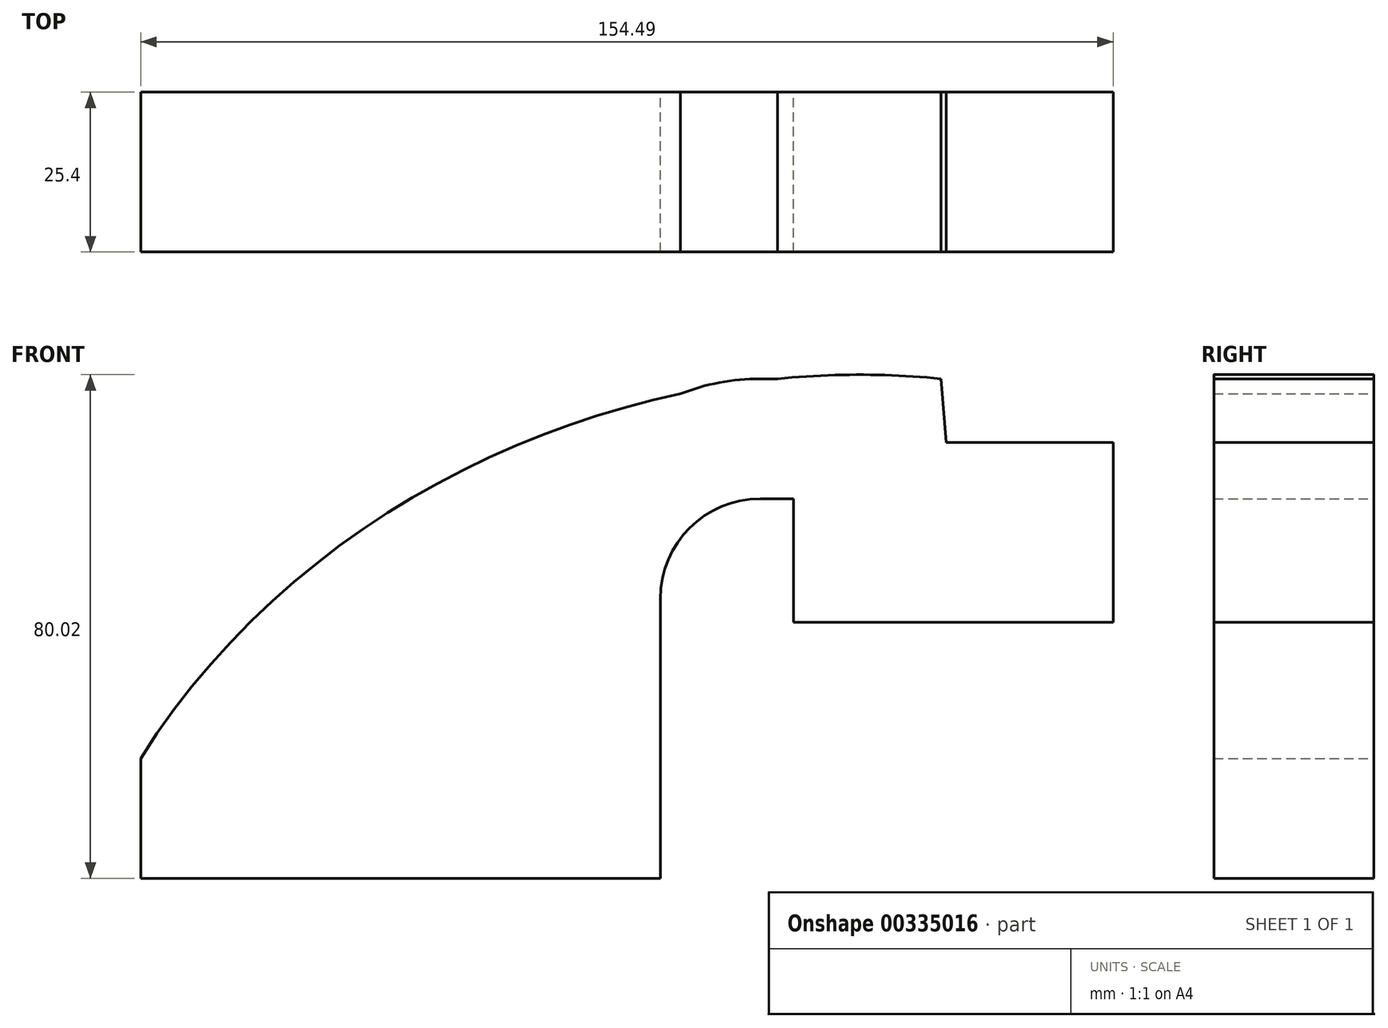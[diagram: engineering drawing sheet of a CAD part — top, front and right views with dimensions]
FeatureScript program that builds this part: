
annotation { "Feature Type Name" : "Feature", "Feature Type Description" : "" }
export const myFeature = defineFeature(function(context is Context, id is Id, definition is map)
    precondition{}
    {
        {
            var Q0;
            Q0=qCreatedBy(makeId("Front.planeOp"),FACE);
            var sketch = newSketch(context, id + "F0", { "sketchPlane" : qUnion([Q0])});
            skLineSegment(sketch, "E0.bottom", {"start": v(-41.28, 9.53) * mm, "end": v(41.27, 9.53) * mm});
            skLineSegment(sketch, "E0.top", {"start": v(-41.28, -9.53) * mm, "end": v(41.28, -9.53) * mm});
            skLineSegment(sketch, "E0.left", {"start": v(-41.28, 9.52) * mm, "end": v(-41.28, -9.53) * mm});
            skLineSegment(sketch, "E0.right", {"start": v(41.28, 9.53) * mm, "end": v(41.28, -9.52) * mm});
            skPoint(sketch, "E0.middle", {"position": v(0, 0) * mm});
            skLineSegment(sketch, "E1.bottom", {"start": v(62.41, 31.17) * mm, "end": v(113.21, 31.17) * mm});
            skLineSegment(sketch, "E1.top", {"start": v(62.41, 59.74) * mm, "end": v(113.21, 59.74) * mm});
            skLineSegment(sketch, "E1.left", {"start": v(62.41, 31.17) * mm, "end": v(62.41, 59.74) * mm});
            skLineSegment(sketch, "E1.right", {"start": v(113.21, 31.17) * mm, "end": v(113.21, 59.74) * mm});
            skPoint(sketch, "E1.middle", {"position": v(87.81, 45.46) * mm});
            skLineSegment(sketch, "E2", {"start": v(41.27, 9.53) * mm, "end": v(41.27, 34.93) * mm});
            skArc(sketch, "E3", {"start": v(41.27, 34.93) * mm, "mid": v(45.92, 46.15) * mm, "end": v(57.15, 50.8) * mm});
            skLineSegment(sketch, "E4", {"start": v(57.15, 50.8) * mm, "end": v(87.43, 50.8) * mm});
            skLineSegment(sketch, "E5.0", {"start": v(57.15, 69.85) * mm, "end": v(85.84, 69.85) * mm});
            skArc(sketch, "E5.1", {"start": v(22.22, 34.93) * mm, "mid": v(32.45, 59.62) * mm, "end": v(57.15, 69.85) * mm});
            skLineSegment(sketch, "E5.2", {"start": v(22.23, 9.53) * mm, "end": v(22.23, 34.93) * mm});
            skLineSegment(sketch, "E6", {"start": v(85.84, 69.85) * mm, "end": v(87.43, 50.8) * mm});
            skFitSpline(sketch, "E7", {"points": [v(-41.28, 9.52) * mm, v(85.84, 69.85) * mm], "startDerivative": vector(80.89, 129.25) * mm, "endDerivative": vector(141.43, -14.33) * mm});
            skLineSegment(sketch, "E8", {"start": v(-14.31, 52.6) * mm, "end": v(-14.31, 52.6) * mm});
            skSolve(sketch);
        }
        {
            var Q0;
            Q0 = qSketchRegion(id + "F0", true);
            extrude(context, id + "F1", {"entities" : qUnion([Q0]), "depth" : 25.4 * mm});
        }
    });
